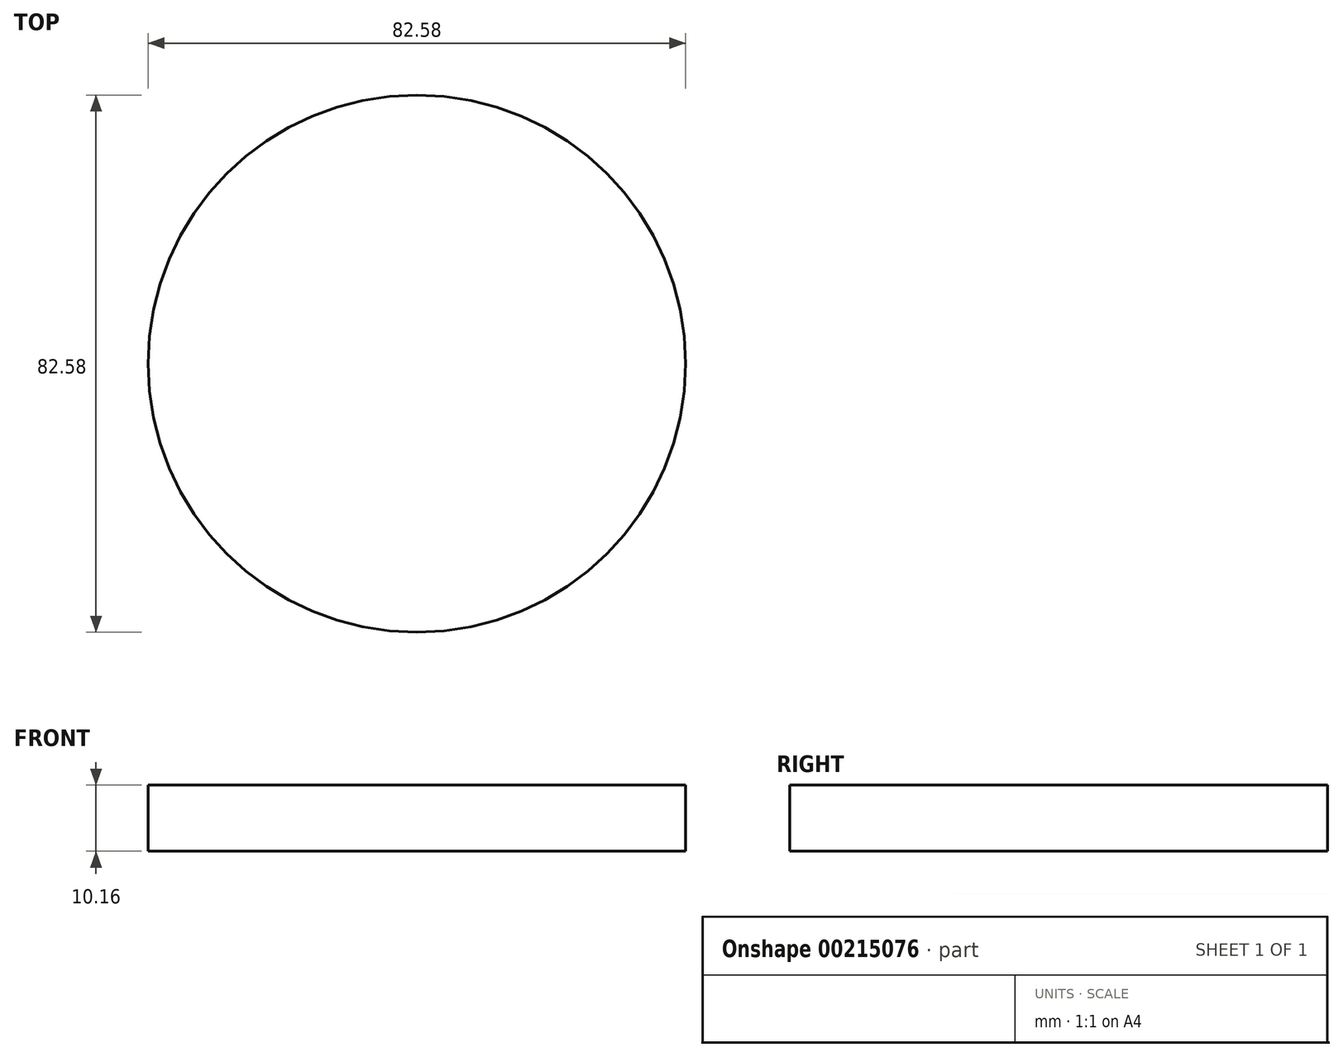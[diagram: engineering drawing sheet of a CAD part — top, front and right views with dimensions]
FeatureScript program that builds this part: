
annotation { "Feature Type Name" : "Feature", "Feature Type Description" : "" }
export const myFeature = defineFeature(function(context is Context, id is Id, definition is map)
    precondition{}
    {
        {
            var Q0;
            Q0=qCreatedBy(makeId("Top.planeOp"),FACE);
            var sketch = newSketch(context, id + "F0", { "sketchPlane" : qUnion([Q0])});
            skCircle(sketch, "E0", {"center": v(0, 0) * mm, "radius": 42.2 * mm});
            skSolve(sketch);
        }
        {
            var Q0;
            Q0=qCreatedBy(makeId("Top.planeOp"),FACE);
            var sketch = newSketch(context, id + "F6", { "sketchPlane" : qUnion([Q0])});
            skCircle(sketch, "E1", {"center": v(0, 0) * mm, "radius": 41.3 * mm});
            skSolve(sketch);
        }
        {
            var Q0;
            Q0=sQuery(id+"F6.wireOp",EDGE,"E1");
            extrude(context, id + "F1", {"bodyType" : ToolBodyType.SURFACE, "surfaceEntities" : qUnion([Q0]), "depth" : 10.16 * mm});
        }
    });
